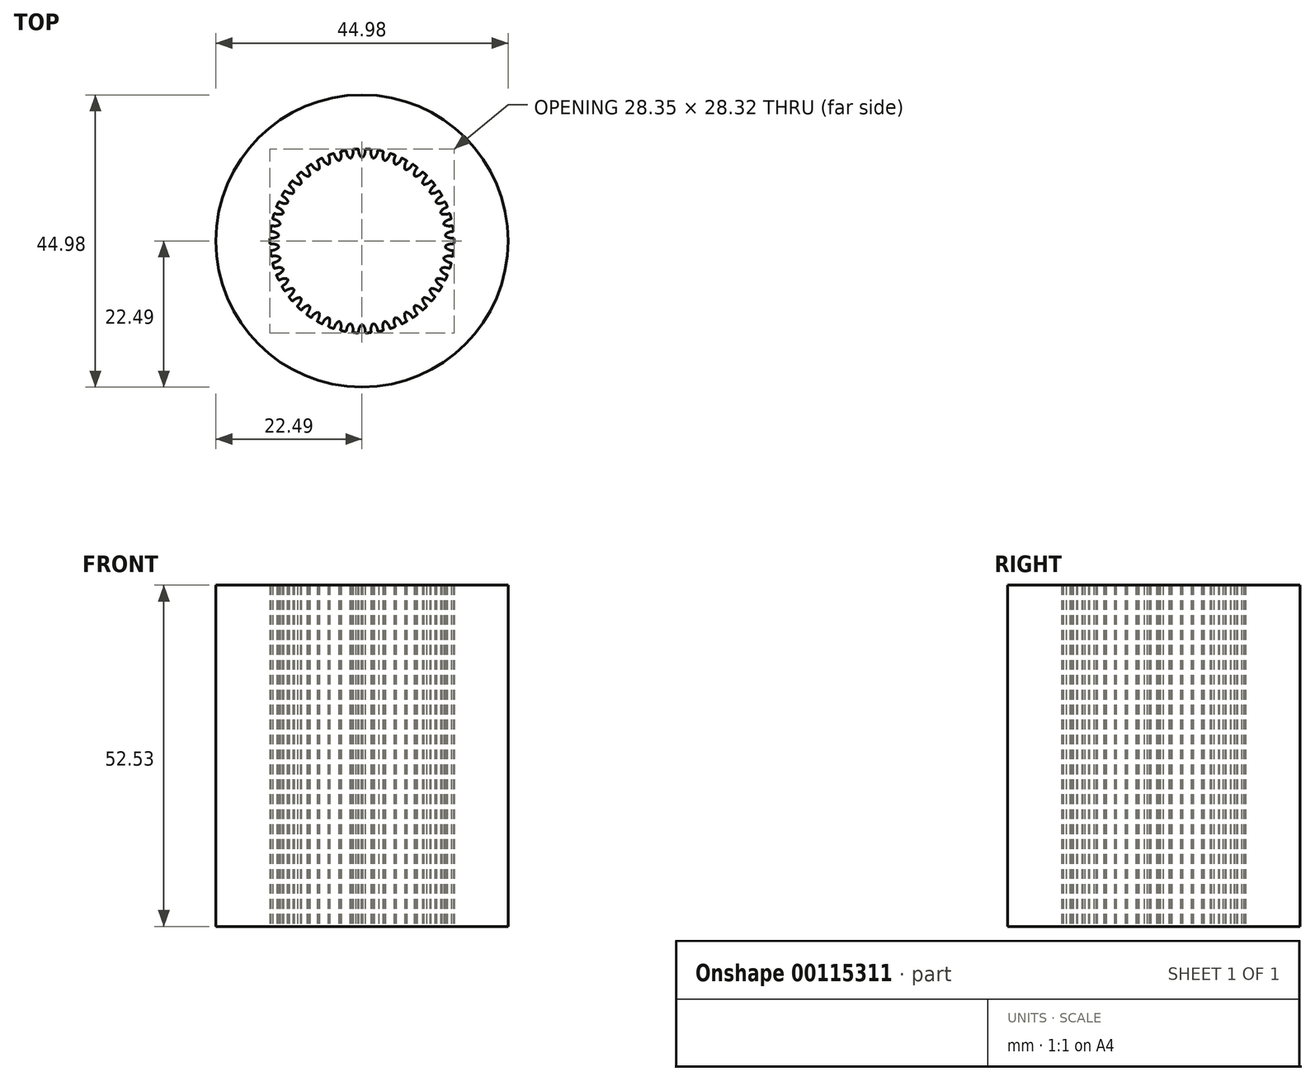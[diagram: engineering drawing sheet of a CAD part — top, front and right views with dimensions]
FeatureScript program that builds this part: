
annotation { "Feature Type Name" : "Feature", "Feature Type Description" : "" }
export const myFeature = defineFeature(function(context is Context, id is Id, definition is map)
    precondition{}
    {
        {
            var Q0;
            Q0=qCreatedBy(makeId("Top.planeOp"),FACE);
            var sketch = newSketch(context, id + "F0", { "sketchPlane" : qUnion([Q0])});
            skArc(sketch, "E0", {"start": v(-1.63, 12.79) * mm, "mid": v(-1.76, 12.77) * mm, "end": v(-1.88, 12.75) * mm});
            skCircle(sketch, "E1", {"center": v(0, 0) * mm, "radius": 22.5 * mm});
            skLineSegment(sketch, "E2", {"start": v(0, 0) * mm, "end": v(0, 14.17) * mm, "construction": true});
            skLineSegment(sketch, "E3", {"start": v(0, 0) * mm, "end": v(-0.97, 14.14) * mm, "construction": true});
            skArc(sketch, "E4", {"start": v(-0.5, 14.02) * mm, "mid": v(-0.54, 14.12) * mm, "end": v(-0.64, 14.16) * mm});
            skArc(sketch, "E5", {"start": v(-0.5, 14.02) * mm, "mid": v(-0.43, 13.42) * mm, "end": v(-0.13, 12.89) * mm});
            skArc(sketch, "E6.MirrorCS", {"start": v(0.5, 14.02) * mm, "mid": v(0.43, 13.42) * mm, "end": v(0.13, 12.89) * mm});
            skArc(sketch, "E7.MirrorCS", {"start": v(0.5, 14.02) * mm, "mid": v(0.54, 14.12) * mm, "end": v(0.64, 14.16) * mm});
            skArc(sketch, "E8.1.0", {"start": v(-1.41, 13.96) * mm, "mid": v(-1.4, 13.35) * mm, "end": v(-1.63, 12.79) * mm});
            skArc(sketch, "E8.1.1", {"start": v(-1.41, 13.96) * mm, "mid": v(-1.39, 14.06) * mm, "end": v(-1.3, 14.11) * mm});
            skArc(sketch, "E8.1.2", {"start": v(-2.4, 13.82) * mm, "mid": v(-2.46, 13.92) * mm, "end": v(-2.56, 13.94) * mm});
            skArc(sketch, "E8.1.3", {"start": v(-2.4, 13.82) * mm, "mid": v(-2.25, 13.23) * mm, "end": v(-1.88, 12.75) * mm});
            skArc(sketch, "E8.2.0", {"start": v(-3.3, 13.64) * mm, "mid": v(-3.2, 13.04) * mm, "end": v(-3.36, 12.45) * mm});
            skArc(sketch, "E8.2.1", {"start": v(-3.3, 13.64) * mm, "mid": v(-3.3, 13.74) * mm, "end": v(-3.2, 13.8) * mm});
            skArc(sketch, "E8.2.2", {"start": v(-4.27, 13.37) * mm, "mid": v(-4.33, 13.45) * mm, "end": v(-4.43, 13.46) * mm});
            skArc(sketch, "E8.2.3", {"start": v(-4.27, 13.37) * mm, "mid": v(-4.03, 12.8) * mm, "end": v(-3.6, 12.38) * mm});
            skArc(sketch, "E8.3.0", {"start": v(-5.13, 13.06) * mm, "mid": v(-4.95, 12.48) * mm, "end": v(-5.02, 11.87) * mm});
            skArc(sketch, "E8.3.1", {"start": v(-5.13, 13.06) * mm, "mid": v(-5.13, 13.17) * mm, "end": v(-5.06, 13.24) * mm});
            skArc(sketch, "E8.3.2", {"start": v(-6.05, 12.66) * mm, "mid": v(-6.12, 12.74) * mm, "end": v(-6.22, 12.73) * mm});
            skArc(sketch, "E8.3.3", {"start": v(-6.05, 12.66) * mm, "mid": v(-5.74, 12.14) * mm, "end": v(-5.25, 11.77) * mm});
            skArc(sketch, "E8.4.0", {"start": v(-6.86, 12.24) * mm, "mid": v(-6.6, 11.69) * mm, "end": v(-6.59, 11.08) * mm});
            skArc(sketch, "E8.4.1", {"start": v(-6.86, 12.24) * mm, "mid": v(-6.88, 12.34) * mm, "end": v(-6.81, 12.43) * mm});
            skArc(sketch, "E8.4.2", {"start": v(-7.72, 11.72) * mm, "mid": v(-7.8, 11.79) * mm, "end": v(-7.9, 11.77) * mm});
            skArc(sketch, "E8.4.3", {"start": v(-7.72, 11.72) * mm, "mid": v(-7.34, 11.24) * mm, "end": v(-6.8, 10.95) * mm});
            skArc(sketch, "E8.5.0", {"start": v(-8.46, 11.2) * mm, "mid": v(-8.13, 10.68) * mm, "end": v(-8.04, 10.08) * mm});
            skArc(sketch, "E8.5.1", {"start": v(-8.46, 11.2) * mm, "mid": v(-8.5, 11.3) * mm, "end": v(-8.44, 11.38) * mm});
            skArc(sketch, "E8.5.2", {"start": v(-9.24, 10.56) * mm, "mid": v(-9.33, 10.61) * mm, "end": v(-9.43, 10.58) * mm});
            skArc(sketch, "E8.5.3", {"start": v(-9.24, 10.56) * mm, "mid": v(-8.8, 10.14) * mm, "end": v(-8.23, 9.92) * mm});
            skArc(sketch, "E8.6.0", {"start": v(-9.9, 9.94) * mm, "mid": v(-9.51, 9.47) * mm, "end": v(-9.33, 8.9) * mm});
            skArc(sketch, "E8.6.1", {"start": v(-9.9, 9.94) * mm, "mid": v(-9.95, 10.03) * mm, "end": v(-9.91, 10.13) * mm});
            skArc(sketch, "E8.6.2", {"start": v(-10.6, 9.2) * mm, "mid": v(-10.69, 9.24) * mm, "end": v(-10.78, 9.2) * mm});
            skArc(sketch, "E8.6.3", {"start": v(-10.6, 9.2) * mm, "mid": v(-10.1, 8.84) * mm, "end": v(-9.5, 8.7) * mm});
            skArc(sketch, "E8.7.0", {"start": v(-11.17, 8.5) * mm, "mid": v(-10.71, 8.09) * mm, "end": v(-10.46, 7.54) * mm});
            skArc(sketch, "E8.7.1", {"start": v(-11.17, 8.5) * mm, "mid": v(-11.23, 8.58) * mm, "end": v(-11.2, 8.68) * mm});
            skArc(sketch, "E8.7.2", {"start": v(-11.75, 7.68) * mm, "mid": v(-11.85, 7.7) * mm, "end": v(-11.93, 7.65) * mm});
            skArc(sketch, "E8.7.3", {"start": v(-11.75, 7.68) * mm, "mid": v(-11.2, 7.39) * mm, "end": v(-10.6, 7.33) * mm});
            skArc(sketch, "E8.8.0", {"start": v(-12.22, 6.9) * mm, "mid": v(-11.72, 6.55) * mm, "end": v(-11.39, 6.04) * mm});
            skArc(sketch, "E8.8.1", {"start": v(-12.22, 6.9) * mm, "mid": v(-12.29, 6.97) * mm, "end": v(-12.28, 7.08) * mm});
            skArc(sketch, "E8.8.2", {"start": v(-12.68, 6) * mm, "mid": v(-12.78, 6.02) * mm, "end": v(-12.86, 5.95) * mm});
            skArc(sketch, "E8.8.3", {"start": v(-12.68, 6) * mm, "mid": v(-12.11, 5.8) * mm, "end": v(-11.5, 5.82) * mm});
            skArc(sketch, "E8.9.0", {"start": v(-13.04, 5.17) * mm, "mid": v(-12.5, 4.9) * mm, "end": v(-12.1, 4.44) * mm});
            skArc(sketch, "E8.9.1", {"start": v(-13.04, 5.17) * mm, "mid": v(-13.12, 5.24) * mm, "end": v(-13.13, 5.34) * mm});
            skArc(sketch, "E8.9.2", {"start": v(-13.38, 4.22) * mm, "mid": v(-13.49, 4.22) * mm, "end": v(-13.55, 4.14) * mm});
            skArc(sketch, "E8.9.3", {"start": v(-13.38, 4.22) * mm, "mid": v(-12.79, 4.09) * mm, "end": v(-12.19, 4.2) * mm});
            skArc(sketch, "E8.10.0", {"start": v(-13.63, 3.35) * mm, "mid": v(-13.05, 3.15) * mm, "end": v(-12.6, 2.75) * mm});
            skArc(sketch, "E8.10.1", {"start": v(-13.63, 3.35) * mm, "mid": v(-13.72, 3.4) * mm, "end": v(-13.73, 3.5) * mm});
            skArc(sketch, "E8.10.2", {"start": v(-13.83, 2.36) * mm, "mid": v(-13.93, 2.35) * mm, "end": v(-14, 2.26) * mm});
            skArc(sketch, "E8.10.3", {"start": v(-13.83, 2.36) * mm, "mid": v(-13.22, 2.3) * mm, "end": v(-12.65, 2.5) * mm});
            skArc(sketch, "E8.11.0", {"start": v(-13.95, 1.46) * mm, "mid": v(-13.36, 1.34) * mm, "end": v(-12.85, 1) * mm});
            skArc(sketch, "E8.11.1", {"start": v(-13.95, 1.46) * mm, "mid": v(-14.05, 1.5) * mm, "end": v(-14.08, 1.6) * mm});
            skArc(sketch, "E8.11.2", {"start": v(-14.02, 0.46) * mm, "mid": v(-14.12, 0.43) * mm, "end": v(-14.17, 0.33) * mm});
            skArc(sketch, "E8.11.3", {"start": v(-14.02, 0.46) * mm, "mid": v(-13.42, 0.49) * mm, "end": v(-12.87, 0.75) * mm});
            skArc(sketch, "E8.12.0", {"start": v(-14.02, -0.46) * mm, "mid": v(-13.42, -0.49) * mm, "end": v(-12.87, -0.75) * mm});
            skArc(sketch, "E8.12.1", {"start": v(-14.02, -0.46) * mm, "mid": v(-14.12, -0.43) * mm, "end": v(-14.17, -0.33) * mm});
            skArc(sketch, "E8.12.2", {"start": v(-13.95, -1.46) * mm, "mid": v(-14.05, -1.5) * mm, "end": v(-14.08, -1.6) * mm});
            skArc(sketch, "E8.12.3", {"start": v(-13.95, -1.46) * mm, "mid": v(-13.36, -1.34) * mm, "end": v(-12.85, -1) * mm});
            skArc(sketch, "E8.13.0", {"start": v(-13.83, -2.36) * mm, "mid": v(-13.22, -2.3) * mm, "end": v(-12.65, -2.5) * mm});
            skArc(sketch, "E8.13.1", {"start": v(-13.83, -2.36) * mm, "mid": v(-13.93, -2.35) * mm, "end": v(-14, -2.26) * mm});
            skArc(sketch, "E8.13.2", {"start": v(-13.63, -3.35) * mm, "mid": v(-13.72, -3.4) * mm, "end": v(-13.73, -3.5) * mm});
            skArc(sketch, "E8.13.3", {"start": v(-13.63, -3.35) * mm, "mid": v(-13.05, -3.15) * mm, "end": v(-12.6, -2.75) * mm});
            skArc(sketch, "E8.14.0", {"start": v(-13.38, -4.22) * mm, "mid": v(-12.79, -4.09) * mm, "end": v(-12.19, -4.2) * mm});
            skArc(sketch, "E8.14.1", {"start": v(-13.38, -4.22) * mm, "mid": v(-13.49, -4.22) * mm, "end": v(-13.55, -4.14) * mm});
            skArc(sketch, "E8.14.2", {"start": v(-13.04, -5.17) * mm, "mid": v(-13.12, -5.24) * mm, "end": v(-13.13, -5.34) * mm});
            skArc(sketch, "E8.14.3", {"start": v(-13.04, -5.17) * mm, "mid": v(-12.5, -4.9) * mm, "end": v(-12.1, -4.44) * mm});
            skArc(sketch, "E8.15.0", {"start": v(-12.68, -6) * mm, "mid": v(-12.11, -5.8) * mm, "end": v(-11.5, -5.82) * mm});
            skArc(sketch, "E8.15.1", {"start": v(-12.68, -6) * mm, "mid": v(-12.78, -6.02) * mm, "end": v(-12.86, -5.95) * mm});
            skArc(sketch, "E8.15.2", {"start": v(-12.22, -6.9) * mm, "mid": v(-12.29, -6.97) * mm, "end": v(-12.28, -7.08) * mm});
            skArc(sketch, "E8.15.3", {"start": v(-12.22, -6.9) * mm, "mid": v(-11.72, -6.55) * mm, "end": v(-11.39, -6.04) * mm});
            skArc(sketch, "E8.16.0", {"start": v(-11.75, -7.68) * mm, "mid": v(-11.2, -7.39) * mm, "end": v(-10.6, -7.33) * mm});
            skArc(sketch, "E8.16.1", {"start": v(-11.75, -7.68) * mm, "mid": v(-11.85, -7.7) * mm, "end": v(-11.93, -7.65) * mm});
            skArc(sketch, "E8.16.2", {"start": v(-11.17, -8.5) * mm, "mid": v(-11.23, -8.58) * mm, "end": v(-11.2, -8.68) * mm});
            skArc(sketch, "E8.16.3", {"start": v(-11.17, -8.5) * mm, "mid": v(-10.71, -8.09) * mm, "end": v(-10.46, -7.54) * mm});
            skArc(sketch, "E8.17.0", {"start": v(-10.6, -9.2) * mm, "mid": v(-10.1, -8.84) * mm, "end": v(-9.5, -8.7) * mm});
            skArc(sketch, "E8.17.1", {"start": v(-10.6, -9.2) * mm, "mid": v(-10.69, -9.24) * mm, "end": v(-10.78, -9.2) * mm});
            skArc(sketch, "E8.17.2", {"start": v(-9.9, -9.94) * mm, "mid": v(-9.95, -10.03) * mm, "end": v(-9.91, -10.13) * mm});
            skArc(sketch, "E8.17.3", {"start": v(-9.9, -9.94) * mm, "mid": v(-9.51, -9.47) * mm, "end": v(-9.33, -8.9) * mm});
            skArc(sketch, "E8.18.0", {"start": v(-9.24, -10.56) * mm, "mid": v(-8.8, -10.14) * mm, "end": v(-8.23, -9.92) * mm});
            skArc(sketch, "E8.18.1", {"start": v(-9.24, -10.56) * mm, "mid": v(-9.33, -10.61) * mm, "end": v(-9.43, -10.58) * mm});
            skArc(sketch, "E8.18.2", {"start": v(-8.46, -11.2) * mm, "mid": v(-8.5, -11.3) * mm, "end": v(-8.44, -11.38) * mm});
            skArc(sketch, "E8.18.3", {"start": v(-8.46, -11.2) * mm, "mid": v(-8.13, -10.68) * mm, "end": v(-8.04, -10.08) * mm});
            skArc(sketch, "E8.19.0", {"start": v(-7.72, -11.72) * mm, "mid": v(-7.34, -11.24) * mm, "end": v(-6.8, -10.95) * mm});
            skArc(sketch, "E8.19.1", {"start": v(-7.72, -11.72) * mm, "mid": v(-7.8, -11.79) * mm, "end": v(-7.9, -11.77) * mm});
            skArc(sketch, "E8.19.2", {"start": v(-6.86, -12.24) * mm, "mid": v(-6.88, -12.34) * mm, "end": v(-6.81, -12.43) * mm});
            skArc(sketch, "E8.19.3", {"start": v(-6.86, -12.24) * mm, "mid": v(-6.6, -11.69) * mm, "end": v(-6.59, -11.08) * mm});
            skArc(sketch, "E8.20.0", {"start": v(-6.05, -12.66) * mm, "mid": v(-5.74, -12.14) * mm, "end": v(-5.25, -11.77) * mm});
            skArc(sketch, "E8.20.1", {"start": v(-6.05, -12.66) * mm, "mid": v(-6.12, -12.74) * mm, "end": v(-6.22, -12.73) * mm});
            skArc(sketch, "E8.20.2", {"start": v(-5.13, -13.06) * mm, "mid": v(-5.13, -13.17) * mm, "end": v(-5.06, -13.24) * mm});
            skArc(sketch, "E8.20.3", {"start": v(-5.13, -13.06) * mm, "mid": v(-4.95, -12.48) * mm, "end": v(-5.02, -11.87) * mm});
            skArc(sketch, "E8.21.0", {"start": v(-4.27, -13.37) * mm, "mid": v(-4.03, -12.8) * mm, "end": v(-3.6, -12.38) * mm});
            skArc(sketch, "E8.21.1", {"start": v(-4.27, -13.37) * mm, "mid": v(-4.33, -13.45) * mm, "end": v(-4.43, -13.46) * mm});
            skArc(sketch, "E8.21.2", {"start": v(-3.3, -13.64) * mm, "mid": v(-3.3, -13.74) * mm, "end": v(-3.2, -13.8) * mm});
            skArc(sketch, "E8.21.3", {"start": v(-3.3, -13.64) * mm, "mid": v(-3.2, -13.04) * mm, "end": v(-3.36, -12.45) * mm});
            skArc(sketch, "E8.22.0", {"start": v(-2.4, -13.82) * mm, "mid": v(-2.25, -13.23) * mm, "end": v(-1.88, -12.75) * mm});
            skArc(sketch, "E8.22.1", {"start": v(-2.4, -13.82) * mm, "mid": v(-2.46, -13.92) * mm, "end": v(-2.56, -13.94) * mm});
            skArc(sketch, "E8.22.2", {"start": v(-1.41, -13.96) * mm, "mid": v(-1.39, -14.06) * mm, "end": v(-1.3, -14.11) * mm});
            skArc(sketch, "E8.22.3", {"start": v(-1.41, -13.96) * mm, "mid": v(-1.4, -13.35) * mm, "end": v(-1.63, -12.79) * mm});
            skArc(sketch, "E8.23.0", {"start": v(-0.5, -14.02) * mm, "mid": v(-0.43, -13.42) * mm, "end": v(-0.13, -12.89) * mm});
            skArc(sketch, "E8.23.1", {"start": v(-0.5, -14.02) * mm, "mid": v(-0.54, -14.12) * mm, "end": v(-0.64, -14.16) * mm});
            skArc(sketch, "E8.23.2", {"start": v(0.5, -14.02) * mm, "mid": v(0.54, -14.12) * mm, "end": v(0.63, -14.16) * mm});
            skArc(sketch, "E8.23.3", {"start": v(0.5, -14.02) * mm, "mid": v(0.43, -13.42) * mm, "end": v(0.13, -12.89) * mm});
            skArc(sketch, "E8.24.0", {"start": v(1.41, -13.96) * mm, "mid": v(1.4, -13.35) * mm, "end": v(1.63, -12.79) * mm});
            skArc(sketch, "E8.24.1", {"start": v(1.41, -13.96) * mm, "mid": v(1.39, -14.06) * mm, "end": v(1.3, -14.11) * mm});
            skArc(sketch, "E8.24.2", {"start": v(2.4, -13.82) * mm, "mid": v(2.46, -13.92) * mm, "end": v(2.56, -13.94) * mm});
            skArc(sketch, "E8.24.3", {"start": v(2.4, -13.82) * mm, "mid": v(2.25, -13.23) * mm, "end": v(1.88, -12.75) * mm});
            skArc(sketch, "E8.25.0", {"start": v(3.3, -13.64) * mm, "mid": v(3.2, -13.04) * mm, "end": v(3.36, -12.45) * mm});
            skArc(sketch, "E8.25.1", {"start": v(3.3, -13.64) * mm, "mid": v(3.3, -13.74) * mm, "end": v(3.2, -13.8) * mm});
            skArc(sketch, "E8.25.2", {"start": v(4.27, -13.37) * mm, "mid": v(4.33, -13.45) * mm, "end": v(4.43, -13.46) * mm});
            skArc(sketch, "E8.25.3", {"start": v(4.27, -13.37) * mm, "mid": v(4.03, -12.8) * mm, "end": v(3.6, -12.38) * mm});
            skArc(sketch, "E8.26.0", {"start": v(5.13, -13.06) * mm, "mid": v(4.95, -12.48) * mm, "end": v(5.02, -11.87) * mm});
            skArc(sketch, "E8.26.1", {"start": v(5.13, -13.06) * mm, "mid": v(5.13, -13.17) * mm, "end": v(5.06, -13.24) * mm});
            skArc(sketch, "E8.26.2", {"start": v(6.05, -12.66) * mm, "mid": v(6.12, -12.74) * mm, "end": v(6.22, -12.73) * mm});
            skArc(sketch, "E8.26.3", {"start": v(6.05, -12.66) * mm, "mid": v(5.74, -12.14) * mm, "end": v(5.25, -11.77) * mm});
            skArc(sketch, "E8.27.0", {"start": v(6.86, -12.24) * mm, "mid": v(6.6, -11.69) * mm, "end": v(6.59, -11.08) * mm});
            skArc(sketch, "E8.27.1", {"start": v(6.86, -12.24) * mm, "mid": v(6.88, -12.34) * mm, "end": v(6.81, -12.43) * mm});
            skArc(sketch, "E8.27.2", {"start": v(7.72, -11.72) * mm, "mid": v(7.8, -11.79) * mm, "end": v(7.9, -11.77) * mm});
            skArc(sketch, "E8.27.3", {"start": v(7.72, -11.72) * mm, "mid": v(7.34, -11.24) * mm, "end": v(6.8, -10.95) * mm});
            skArc(sketch, "E8.28.0", {"start": v(8.46, -11.2) * mm, "mid": v(8.13, -10.68) * mm, "end": v(8.04, -10.08) * mm});
            skArc(sketch, "E8.28.1", {"start": v(8.46, -11.2) * mm, "mid": v(8.5, -11.3) * mm, "end": v(8.44, -11.38) * mm});
            skArc(sketch, "E8.28.2", {"start": v(9.24, -10.56) * mm, "mid": v(9.33, -10.61) * mm, "end": v(9.43, -10.58) * mm});
            skArc(sketch, "E8.28.3", {"start": v(9.24, -10.56) * mm, "mid": v(8.8, -10.14) * mm, "end": v(8.23, -9.92) * mm});
            skArc(sketch, "E8.29.0", {"start": v(9.9, -9.94) * mm, "mid": v(9.51, -9.47) * mm, "end": v(9.33, -8.9) * mm});
            skArc(sketch, "E8.29.1", {"start": v(9.9, -9.94) * mm, "mid": v(9.95, -10.03) * mm, "end": v(9.91, -10.13) * mm});
            skArc(sketch, "E8.29.2", {"start": v(10.6, -9.2) * mm, "mid": v(10.69, -9.24) * mm, "end": v(10.78, -9.2) * mm});
            skArc(sketch, "E8.29.3", {"start": v(10.6, -9.2) * mm, "mid": v(10.1, -8.84) * mm, "end": v(9.5, -8.7) * mm});
            skArc(sketch, "E8.30.0", {"start": v(11.17, -8.5) * mm, "mid": v(10.71, -8.09) * mm, "end": v(10.46, -7.54) * mm});
            skArc(sketch, "E8.30.1", {"start": v(11.17, -8.5) * mm, "mid": v(11.23, -8.58) * mm, "end": v(11.2, -8.68) * mm});
            skArc(sketch, "E8.30.2", {"start": v(11.75, -7.68) * mm, "mid": v(11.85, -7.7) * mm, "end": v(11.93, -7.65) * mm});
            skArc(sketch, "E8.30.3", {"start": v(11.75, -7.68) * mm, "mid": v(11.2, -7.39) * mm, "end": v(10.6, -7.33) * mm});
            skArc(sketch, "E8.31.0", {"start": v(12.22, -6.9) * mm, "mid": v(11.72, -6.55) * mm, "end": v(11.39, -6.04) * mm});
            skArc(sketch, "E8.31.1", {"start": v(12.22, -6.9) * mm, "mid": v(12.29, -6.97) * mm, "end": v(12.28, -7.08) * mm});
            skArc(sketch, "E8.31.2", {"start": v(12.68, -6) * mm, "mid": v(12.78, -6.02) * mm, "end": v(12.86, -5.95) * mm});
            skArc(sketch, "E8.31.3", {"start": v(12.68, -6) * mm, "mid": v(12.11, -5.8) * mm, "end": v(11.5, -5.82) * mm});
            skArc(sketch, "E8.32.0", {"start": v(13.04, -5.17) * mm, "mid": v(12.5, -4.9) * mm, "end": v(12.1, -4.44) * mm});
            skArc(sketch, "E8.32.1", {"start": v(13.04, -5.17) * mm, "mid": v(13.12, -5.24) * mm, "end": v(13.13, -5.34) * mm});
            skArc(sketch, "E8.32.2", {"start": v(13.38, -4.22) * mm, "mid": v(13.49, -4.22) * mm, "end": v(13.55, -4.14) * mm});
            skArc(sketch, "E8.32.3", {"start": v(13.38, -4.22) * mm, "mid": v(12.79, -4.09) * mm, "end": v(12.19, -4.2) * mm});
            skArc(sketch, "E8.33.0", {"start": v(13.63, -3.35) * mm, "mid": v(13.05, -3.15) * mm, "end": v(12.6, -2.75) * mm});
            skArc(sketch, "E8.33.1", {"start": v(13.63, -3.35) * mm, "mid": v(13.72, -3.4) * mm, "end": v(13.73, -3.5) * mm});
            skArc(sketch, "E8.33.2", {"start": v(13.83, -2.36) * mm, "mid": v(13.93, -2.35) * mm, "end": v(14, -2.26) * mm});
            skArc(sketch, "E8.33.3", {"start": v(13.83, -2.36) * mm, "mid": v(13.22, -2.3) * mm, "end": v(12.65, -2.5) * mm});
            skArc(sketch, "E8.34.0", {"start": v(13.95, -1.46) * mm, "mid": v(13.36, -1.34) * mm, "end": v(12.85, -1) * mm});
            skArc(sketch, "E8.34.1", {"start": v(13.95, -1.46) * mm, "mid": v(14.05, -1.5) * mm, "end": v(14.08, -1.6) * mm});
            skArc(sketch, "E8.34.2", {"start": v(14.02, -0.46) * mm, "mid": v(14.12, -0.43) * mm, "end": v(14.17, -0.33) * mm});
            skArc(sketch, "E8.34.3", {"start": v(14.02, -0.46) * mm, "mid": v(13.42, -0.49) * mm, "end": v(12.87, -0.75) * mm});
            skArc(sketch, "E8.35.0", {"start": v(14.02, 0.46) * mm, "mid": v(13.42, 0.49) * mm, "end": v(12.87, 0.75) * mm});
            skArc(sketch, "E8.35.1", {"start": v(14.02, 0.46) * mm, "mid": v(14.12, 0.43) * mm, "end": v(14.17, 0.33) * mm});
            skArc(sketch, "E8.35.2", {"start": v(13.95, 1.46) * mm, "mid": v(14.05, 1.5) * mm, "end": v(14.08, 1.6) * mm});
            skArc(sketch, "E8.35.3", {"start": v(13.95, 1.46) * mm, "mid": v(13.36, 1.34) * mm, "end": v(12.85, 1) * mm});
            skArc(sketch, "E8.36.0", {"start": v(13.83, 2.36) * mm, "mid": v(13.22, 2.3) * mm, "end": v(12.65, 2.5) * mm});
            skArc(sketch, "E8.36.1", {"start": v(13.83, 2.36) * mm, "mid": v(13.93, 2.35) * mm, "end": v(14, 2.26) * mm});
            skArc(sketch, "E8.36.2", {"start": v(13.63, 3.35) * mm, "mid": v(13.72, 3.4) * mm, "end": v(13.73, 3.5) * mm});
            skArc(sketch, "E8.36.3", {"start": v(13.63, 3.35) * mm, "mid": v(13.05, 3.15) * mm, "end": v(12.6, 2.75) * mm});
            skArc(sketch, "E8.37.0", {"start": v(13.38, 4.22) * mm, "mid": v(12.79, 4.09) * mm, "end": v(12.19, 4.2) * mm});
            skArc(sketch, "E8.37.1", {"start": v(13.38, 4.22) * mm, "mid": v(13.49, 4.22) * mm, "end": v(13.55, 4.14) * mm});
            skArc(sketch, "E8.37.2", {"start": v(13.04, 5.17) * mm, "mid": v(13.12, 5.24) * mm, "end": v(13.13, 5.34) * mm});
            skArc(sketch, "E8.37.3", {"start": v(13.04, 5.17) * mm, "mid": v(12.5, 4.9) * mm, "end": v(12.1, 4.44) * mm});
            skArc(sketch, "E8.38.0", {"start": v(12.68, 6) * mm, "mid": v(12.11, 5.8) * mm, "end": v(11.5, 5.82) * mm});
            skArc(sketch, "E8.38.1", {"start": v(12.68, 6) * mm, "mid": v(12.78, 6.02) * mm, "end": v(12.86, 5.95) * mm});
            skArc(sketch, "E8.38.2", {"start": v(12.22, 6.9) * mm, "mid": v(12.29, 6.97) * mm, "end": v(12.28, 7.08) * mm});
            skArc(sketch, "E8.38.3", {"start": v(12.22, 6.9) * mm, "mid": v(11.72, 6.55) * mm, "end": v(11.39, 6.04) * mm});
            skArc(sketch, "E8.39.0", {"start": v(11.75, 7.68) * mm, "mid": v(11.2, 7.39) * mm, "end": v(10.6, 7.33) * mm});
            skArc(sketch, "E8.39.1", {"start": v(11.75, 7.68) * mm, "mid": v(11.85, 7.7) * mm, "end": v(11.93, 7.65) * mm});
            skArc(sketch, "E8.39.2", {"start": v(11.17, 8.5) * mm, "mid": v(11.23, 8.58) * mm, "end": v(11.2, 8.68) * mm});
            skArc(sketch, "E8.39.3", {"start": v(11.17, 8.5) * mm, "mid": v(10.71, 8.09) * mm, "end": v(10.46, 7.54) * mm});
            skArc(sketch, "E8.40.0", {"start": v(10.6, 9.2) * mm, "mid": v(10.1, 8.84) * mm, "end": v(9.5, 8.7) * mm});
            skArc(sketch, "E8.40.1", {"start": v(10.6, 9.2) * mm, "mid": v(10.69, 9.24) * mm, "end": v(10.78, 9.2) * mm});
            skArc(sketch, "E8.40.2", {"start": v(9.9, 9.94) * mm, "mid": v(9.95, 10.03) * mm, "end": v(9.91, 10.13) * mm});
            skArc(sketch, "E8.40.3", {"start": v(9.9, 9.94) * mm, "mid": v(9.51, 9.47) * mm, "end": v(9.33, 8.9) * mm});
            skArc(sketch, "E8.41.0", {"start": v(9.24, 10.56) * mm, "mid": v(8.8, 10.14) * mm, "end": v(8.23, 9.92) * mm});
            skArc(sketch, "E8.41.1", {"start": v(9.24, 10.56) * mm, "mid": v(9.33, 10.61) * mm, "end": v(9.43, 10.58) * mm});
            skArc(sketch, "E8.41.2", {"start": v(8.46, 11.2) * mm, "mid": v(8.5, 11.3) * mm, "end": v(8.44, 11.38) * mm});
            skArc(sketch, "E8.41.3", {"start": v(8.46, 11.2) * mm, "mid": v(8.13, 10.68) * mm, "end": v(8.04, 10.08) * mm});
            skArc(sketch, "E8.42.0", {"start": v(7.72, 11.72) * mm, "mid": v(7.34, 11.24) * mm, "end": v(6.8, 10.95) * mm});
            skArc(sketch, "E8.42.1", {"start": v(7.72, 11.72) * mm, "mid": v(7.8, 11.79) * mm, "end": v(7.9, 11.77) * mm});
            skArc(sketch, "E8.42.2", {"start": v(6.86, 12.24) * mm, "mid": v(6.88, 12.34) * mm, "end": v(6.81, 12.43) * mm});
            skArc(sketch, "E8.42.3", {"start": v(6.86, 12.24) * mm, "mid": v(6.6, 11.69) * mm, "end": v(6.59, 11.08) * mm});
            skArc(sketch, "E8.43.0", {"start": v(6.05, 12.66) * mm, "mid": v(5.74, 12.14) * mm, "end": v(5.25, 11.77) * mm});
            skArc(sketch, "E8.43.1", {"start": v(6.05, 12.66) * mm, "mid": v(6.12, 12.74) * mm, "end": v(6.22, 12.73) * mm});
            skArc(sketch, "E8.43.2", {"start": v(5.13, 13.06) * mm, "mid": v(5.13, 13.17) * mm, "end": v(5.06, 13.24) * mm});
            skArc(sketch, "E8.43.3", {"start": v(5.13, 13.06) * mm, "mid": v(4.95, 12.48) * mm, "end": v(5.02, 11.87) * mm});
            skArc(sketch, "E8.44.0", {"start": v(4.27, 13.37) * mm, "mid": v(4.03, 12.8) * mm, "end": v(3.6, 12.38) * mm});
            skArc(sketch, "E8.44.1", {"start": v(4.27, 13.37) * mm, "mid": v(4.33, 13.45) * mm, "end": v(4.43, 13.46) * mm});
            skArc(sketch, "E8.44.2", {"start": v(3.3, 13.64) * mm, "mid": v(3.3, 13.74) * mm, "end": v(3.2, 13.8) * mm});
            skArc(sketch, "E8.44.3", {"start": v(3.3, 13.64) * mm, "mid": v(3.2, 13.04) * mm, "end": v(3.36, 12.45) * mm});
            skArc(sketch, "E8.45.0", {"start": v(2.4, 13.82) * mm, "mid": v(2.25, 13.23) * mm, "end": v(1.88, 12.75) * mm});
            skArc(sketch, "E8.45.1", {"start": v(2.4, 13.82) * mm, "mid": v(2.46, 13.92) * mm, "end": v(2.56, 13.94) * mm});
            skArc(sketch, "E8.45.2", {"start": v(1.41, 13.96) * mm, "mid": v(1.39, 14.06) * mm, "end": v(1.3, 14.11) * mm});
            skArc(sketch, "E8.45.3", {"start": v(1.41, 13.96) * mm, "mid": v(1.4, 13.35) * mm, "end": v(1.63, 12.79) * mm});
            skArc(sketch, "E9.trimOffspring", {"start": v(0.13, 12.89) * mm, "mid": v(0, 12.9) * mm, "end": v(-0.13, 12.89) * mm});
            skArc(sketch, "E10.trimOffspring", {"start": v(1.88, 12.75) * mm, "mid": v(1.76, 12.77) * mm, "end": v(1.63, 12.79) * mm});
            skArc(sketch, "E11.trimOffspring", {"start": v(3.6, 12.38) * mm, "mid": v(3.48, 12.41) * mm, "end": v(3.36, 12.45) * mm});
            skArc(sketch, "E12.trimOffspring", {"start": v(5.25, 11.77) * mm, "mid": v(5.14, 11.82) * mm, "end": v(5.02, 11.87) * mm});
            skArc(sketch, "E13.trimOffspring", {"start": v(6.8, 10.95) * mm, "mid": v(6.7, 11.01) * mm, "end": v(6.59, 11.08) * mm});
            skArc(sketch, "E14.trimOffspring", {"start": v(8.23, 9.92) * mm, "mid": v(8.14, 10) * mm, "end": v(8.04, 10.08) * mm});
            skArc(sketch, "E15.trimOffspring", {"start": v(9.5, 8.7) * mm, "mid": v(9.42, 8.8) * mm, "end": v(9.33, 8.9) * mm});
            skArc(sketch, "E16.trimOffspring", {"start": v(10.6, 7.33) * mm, "mid": v(10.53, 7.43) * mm, "end": v(10.46, 7.54) * mm});
            skArc(sketch, "E17.trimOffspring", {"start": v(11.5, 5.82) * mm, "mid": v(11.45, 5.93) * mm, "end": v(11.39, 6.04) * mm});
            skArc(sketch, "E18.trimOffspring", {"start": v(12.19, 4.2) * mm, "mid": v(12.15, 4.32) * mm, "end": v(12.1, 4.44) * mm});
            skArc(sketch, "E19.trimOffspring", {"start": v(12.65, 2.5) * mm, "mid": v(12.62, 2.62) * mm, "end": v(12.6, 2.75) * mm});
            skArc(sketch, "E20.trimOffspring", {"start": v(12.87, 0.75) * mm, "mid": v(12.86, 0.88) * mm, "end": v(12.85, 1) * mm});
            skArc(sketch, "E21.trimOffspring", {"start": v(12.85, -1) * mm, "mid": v(12.86, -0.88) * mm, "end": v(12.87, -0.75) * mm});
            skArc(sketch, "E22.trimOffspring", {"start": v(12.1, -4.44) * mm, "mid": v(12.15, -4.32) * mm, "end": v(12.19, -4.2) * mm});
            skArc(sketch, "E23.trimOffspring", {"start": v(11.39, -6.04) * mm, "mid": v(11.45, -5.93) * mm, "end": v(11.5, -5.82) * mm});
            skArc(sketch, "E24.trimOffspring", {"start": v(10.46, -7.54) * mm, "mid": v(10.53, -7.43) * mm, "end": v(10.6, -7.33) * mm});
            skArc(sketch, "E25.trimOffspring", {"start": v(1.3, 14.11) * mm, "mid": v(0.97, 14.14) * mm, "end": v(0.64, 14.16) * mm});
            skArc(sketch, "E26.trimOffspring", {"start": v(11.2, 8.68) * mm, "mid": v(11, 8.94) * mm, "end": v(10.78, 9.2) * mm});
            skArc(sketch, "E27.trimOffspring", {"start": v(12.28, 7.08) * mm, "mid": v(12.1, 7.36) * mm, "end": v(11.93, 7.65) * mm});
            skArc(sketch, "E28.trimOffspring", {"start": v(5.06, 13.24) * mm, "mid": v(4.75, 13.35) * mm, "end": v(4.43, 13.46) * mm});
            skArc(sketch, "E29.trimOffspring", {"start": v(6.81, 12.43) * mm, "mid": v(6.52, 12.58) * mm, "end": v(6.22, 12.73) * mm});
            skArc(sketch, "E30.trimOffspring", {"start": v(8.44, 11.38) * mm, "mid": v(8.17, 11.58) * mm, "end": v(7.9, 11.77) * mm});
            skArc(sketch, "E31.trimOffspring", {"start": v(9.91, 10.13) * mm, "mid": v(9.67, 10.36) * mm, "end": v(9.43, 10.58) * mm});
            skArc(sketch, "E32.trimOffspring", {"start": v(13.13, 5.34) * mm, "mid": v(13, 5.65) * mm, "end": v(12.86, 5.95) * mm});
            skArc(sketch, "E33.trimOffspring", {"start": v(13.73, 3.5) * mm, "mid": v(13.65, 3.82) * mm, "end": v(13.55, 4.14) * mm});
            skArc(sketch, "E34.trimOffspring", {"start": v(14.08, 1.6) * mm, "mid": v(14.04, 1.93) * mm, "end": v(14, 2.26) * mm});
            skArc(sketch, "E35.trimOffspring", {"start": v(14.17, -0.33) * mm, "mid": v(14.17, 0) * mm, "end": v(14.17, 0.33) * mm});
            skArc(sketch, "E36.trimOffspring", {"start": v(14, -2.26) * mm, "mid": v(14.04, -1.93) * mm, "end": v(14.08, -1.6) * mm});
            skArc(sketch, "E37.trimOffspring", {"start": v(13.55, -4.14) * mm, "mid": v(13.65, -3.82) * mm, "end": v(13.73, -3.5) * mm});
            skArc(sketch, "E38.trimOffspring", {"start": v(12.86, -5.95) * mm, "mid": v(13, -5.65) * mm, "end": v(13.13, -5.34) * mm});
            skArc(sketch, "E39.trimOffspring", {"start": v(11.93, -7.65) * mm, "mid": v(12.1, -7.36) * mm, "end": v(12.28, -7.08) * mm});
            skArc(sketch, "E40.trimOffspring", {"start": v(10.78, -9.2) * mm, "mid": v(11, -8.94) * mm, "end": v(11.2, -8.68) * mm});
            skArc(sketch, "E41.trimOffspring", {"start": v(9.33, -8.9) * mm, "mid": v(9.42, -8.8) * mm, "end": v(9.5, -8.7) * mm});
            skArc(sketch, "E42.trimOffspring", {"start": v(9.43, -10.58) * mm, "mid": v(9.67, -10.36) * mm, "end": v(9.91, -10.13) * mm});
            skArc(sketch, "E43.trimOffspring", {"start": v(8.04, -10.08) * mm, "mid": v(8.14, -10) * mm, "end": v(8.23, -9.92) * mm});
            skArc(sketch, "E44.trimOffspring", {"start": v(7.9, -11.77) * mm, "mid": v(8.17, -11.58) * mm, "end": v(8.44, -11.38) * mm});
            skArc(sketch, "E45.trimOffspring", {"start": v(6.59, -11.08) * mm, "mid": v(6.7, -11.01) * mm, "end": v(6.8, -10.95) * mm});
            skArc(sketch, "E46.trimOffspring", {"start": v(6.22, -12.73) * mm, "mid": v(6.52, -12.58) * mm, "end": v(6.81, -12.43) * mm});
            skArc(sketch, "E47.trimOffspring", {"start": v(5.02, -11.87) * mm, "mid": v(5.14, -11.82) * mm, "end": v(5.25, -11.77) * mm});
            skArc(sketch, "E48.trimOffspring", {"start": v(4.43, -13.46) * mm, "mid": v(4.75, -13.35) * mm, "end": v(5.06, -13.24) * mm});
            skArc(sketch, "E49.trimOffspring", {"start": v(3.36, -12.45) * mm, "mid": v(3.48, -12.41) * mm, "end": v(3.6, -12.38) * mm});
            skArc(sketch, "E50.trimOffspring", {"start": v(2.56, -13.94) * mm, "mid": v(2.88, -13.88) * mm, "end": v(3.2, -13.8) * mm});
            skArc(sketch, "E51.trimOffspring", {"start": v(1.63, -12.79) * mm, "mid": v(1.76, -12.77) * mm, "end": v(1.88, -12.75) * mm});
            skArc(sketch, "E52.trimOffspring", {"start": v(0.63, -14.16) * mm, "mid": v(0.97, -14.14) * mm, "end": v(1.3, -14.11) * mm});
            skArc(sketch, "E53.trimOffspring", {"start": v(-0.13, -12.89) * mm, "mid": v(0, -12.9) * mm, "end": v(0.13, -12.89) * mm});
            skArc(sketch, "E54.trimOffspring", {"start": v(-1.3, -14.11) * mm, "mid": v(-0.97, -14.14) * mm, "end": v(-0.63, -14.16) * mm});
            skArc(sketch, "E55.trimOffspring", {"start": v(-1.88, -12.75) * mm, "mid": v(-1.76, -12.77) * mm, "end": v(-1.63, -12.79) * mm});
            skArc(sketch, "E56.trimOffspring", {"start": v(-3.2, -13.8) * mm, "mid": v(-2.88, -13.88) * mm, "end": v(-2.56, -13.94) * mm});
            skArc(sketch, "E57.trimOffspring", {"start": v(-3.6, -12.38) * mm, "mid": v(-3.48, -12.41) * mm, "end": v(-3.36, -12.45) * mm});
            skArc(sketch, "E58.trimOffspring", {"start": v(-5.06, -13.24) * mm, "mid": v(-4.75, -13.35) * mm, "end": v(-4.43, -13.46) * mm});
            skArc(sketch, "E59.trimOffspring", {"start": v(-5.25, -11.77) * mm, "mid": v(-5.14, -11.82) * mm, "end": v(-5.02, -11.87) * mm});
            skArc(sketch, "E60.trimOffspring", {"start": v(-6.81, -12.43) * mm, "mid": v(-6.52, -12.58) * mm, "end": v(-6.22, -12.73) * mm});
            skArc(sketch, "E61.trimOffspring", {"start": v(-6.8, -10.95) * mm, "mid": v(-6.7, -11.01) * mm, "end": v(-6.59, -11.08) * mm});
            skArc(sketch, "E62.trimOffspring", {"start": v(-8.44, -11.38) * mm, "mid": v(-8.17, -11.58) * mm, "end": v(-7.9, -11.77) * mm});
            skArc(sketch, "E63.trimOffspring", {"start": v(-8.23, -9.92) * mm, "mid": v(-8.14, -10) * mm, "end": v(-8.04, -10.08) * mm});
            skArc(sketch, "E64.trimOffspring", {"start": v(-9.91, -10.13) * mm, "mid": v(-9.67, -10.36) * mm, "end": v(-9.43, -10.58) * mm});
            skArc(sketch, "E65.trimOffspring", {"start": v(-9.5, -8.7) * mm, "mid": v(-9.42, -8.8) * mm, "end": v(-9.33, -8.9) * mm});
            skArc(sketch, "E66.trimOffspring", {"start": v(-11.2, -8.68) * mm, "mid": v(-11, -8.94) * mm, "end": v(-10.78, -9.2) * mm});
            skArc(sketch, "E67.trimOffspring", {"start": v(-10.6, -7.33) * mm, "mid": v(-10.53, -7.43) * mm, "end": v(-10.46, -7.54) * mm});
            skArc(sketch, "E68.trimOffspring", {"start": v(-12.28, -7.08) * mm, "mid": v(-12.1, -7.36) * mm, "end": v(-11.93, -7.65) * mm});
            skArc(sketch, "E69.trimOffspring", {"start": v(-13.13, -5.34) * mm, "mid": v(-13, -5.65) * mm, "end": v(-12.86, -5.95) * mm});
            skArc(sketch, "E70.trimOffspring", {"start": v(-13.73, -3.5) * mm, "mid": v(-13.65, -3.82) * mm, "end": v(-13.55, -4.14) * mm});
            skArc(sketch, "E71.trimOffspring", {"start": v(-12.19, -4.2) * mm, "mid": v(-12.15, -4.32) * mm, "end": v(-12.1, -4.44) * mm});
            skArc(sketch, "E72.trimOffspring", {"start": v(-12.65, -2.5) * mm, "mid": v(-12.62, -2.62) * mm, "end": v(-12.6, -2.75) * mm});
            skArc(sketch, "E73.trimOffspring", {"start": v(-12.87, -0.75) * mm, "mid": v(-12.86, -0.88) * mm, "end": v(-12.85, -1) * mm});
            skArc(sketch, "E74.trimOffspring", {"start": v(-14.08, -1.6) * mm, "mid": v(-14.04, -1.93) * mm, "end": v(-14, -2.26) * mm});
            skArc(sketch, "E75.trimOffspring", {"start": v(-14.17, 0.33) * mm, "mid": v(-14.17, 0) * mm, "end": v(-14.17, -0.33) * mm});
            skArc(sketch, "E76.trimOffspring", {"start": v(-12.85, 1) * mm, "mid": v(-12.86, 0.88) * mm, "end": v(-12.87, 0.75) * mm});
            skArc(sketch, "E77.trimOffspring", {"start": v(-14, 2.26) * mm, "mid": v(-14.04, 1.93) * mm, "end": v(-14.08, 1.6) * mm});
            skArc(sketch, "E78.trimOffspring", {"start": v(-12.6, 2.75) * mm, "mid": v(-12.62, 2.62) * mm, "end": v(-12.65, 2.5) * mm});
            skArc(sketch, "E79.trimOffspring", {"start": v(-13.55, 4.14) * mm, "mid": v(-13.65, 3.82) * mm, "end": v(-13.73, 3.5) * mm});
            skArc(sketch, "E80.trimOffspring", {"start": v(-12.1, 4.44) * mm, "mid": v(-12.15, 4.32) * mm, "end": v(-12.19, 4.2) * mm});
            skArc(sketch, "E81.trimOffspring", {"start": v(-12.86, 5.95) * mm, "mid": v(-13, 5.65) * mm, "end": v(-13.13, 5.34) * mm});
            skArc(sketch, "E82.trimOffspring", {"start": v(-11.93, 7.65) * mm, "mid": v(-12.1, 7.36) * mm, "end": v(-12.28, 7.08) * mm});
            skArc(sketch, "E83.trimOffspring", {"start": v(-10.46, 7.54) * mm, "mid": v(-10.53, 7.43) * mm, "end": v(-10.6, 7.33) * mm});
            skArc(sketch, "E84.trimOffspring", {"start": v(-10.78, 9.2) * mm, "mid": v(-11, 8.94) * mm, "end": v(-11.2, 8.68) * mm});
            skArc(sketch, "E85.trimOffspring", {"start": v(-9.43, 10.58) * mm, "mid": v(-9.67, 10.36) * mm, "end": v(-9.91, 10.13) * mm});
            skArc(sketch, "E86.trimOffspring", {"start": v(-9.33, 8.9) * mm, "mid": v(-9.42, 8.8) * mm, "end": v(-9.5, 8.7) * mm});
            skArc(sketch, "E87.trimOffspring", {"start": v(-8.04, 10.08) * mm, "mid": v(-8.14, 10) * mm, "end": v(-8.23, 9.92) * mm});
            skArc(sketch, "E88.trimOffspring", {"start": v(-7.9, 11.77) * mm, "mid": v(-8.17, 11.58) * mm, "end": v(-8.44, 11.38) * mm});
            skArc(sketch, "E89.trimOffspring", {"start": v(-6.59, 11.08) * mm, "mid": v(-6.7, 11.01) * mm, "end": v(-6.8, 10.95) * mm});
            skArc(sketch, "E90.trimOffspring", {"start": v(-6.22, 12.73) * mm, "mid": v(-6.52, 12.58) * mm, "end": v(-6.81, 12.43) * mm});
            skArc(sketch, "E91.trimOffspring", {"start": v(-5.02, 11.87) * mm, "mid": v(-5.14, 11.82) * mm, "end": v(-5.25, 11.77) * mm});
            skArc(sketch, "E92.trimOffspring", {"start": v(-3.36, 12.45) * mm, "mid": v(-3.48, 12.41) * mm, "end": v(-3.6, 12.38) * mm});
            skArc(sketch, "E93.trimOffspring", {"start": v(-4.43, 13.46) * mm, "mid": v(-4.75, 13.35) * mm, "end": v(-5.06, 13.24) * mm});
            skArc(sketch, "E94.trimOffspring", {"start": v(-2.56, 13.94) * mm, "mid": v(-2.88, 13.88) * mm, "end": v(-3.2, 13.8) * mm});
            skArc(sketch, "E95.trimOffspring", {"start": v(-0.97, 14.14) * mm, "mid": v(-1.13, 14.13) * mm, "end": v(-1.3, 14.11) * mm});
            skLineSegment(sketch, "E96", {"start": v(-0.97, 14.14) * mm, "end": v(-0.64, 14.16) * mm});
            skLineSegment(sketch, "E97", {"start": v(-11.39, 6.04) * mm, "end": v(-11.5, 5.82) * mm});
            skLineSegment(sketch, "E98", {"start": v(12.65, -2.5) * mm, "end": v(12.6, -2.75) * mm});
            skLineSegment(sketch, "E99", {"start": v(-11.39, -6.04) * mm, "end": v(-11.5, -5.82) * mm});
            skLineSegment(sketch, "E100", {"start": v(2.56, 13.94) * mm, "end": v(3.2, 13.8) * mm});
            skSolve(sketch);
        }
        {
            var Q0;
            Q0=makeQuery(id+"F0.imprint","IMPRINT",FACE,{"disambiguationData":[TD([[makeQuery(id+"F0.imprint","IMPRINT",EDGE,{"derivedFrom":sQuery(id+"F0.wireOp",EDGE,"E0")}),-1.0]])]});
            extrude(context, id + "F1", {"entities" : qUnion([Q0]), "depth" : 52.53 * mm});
        }
    });
